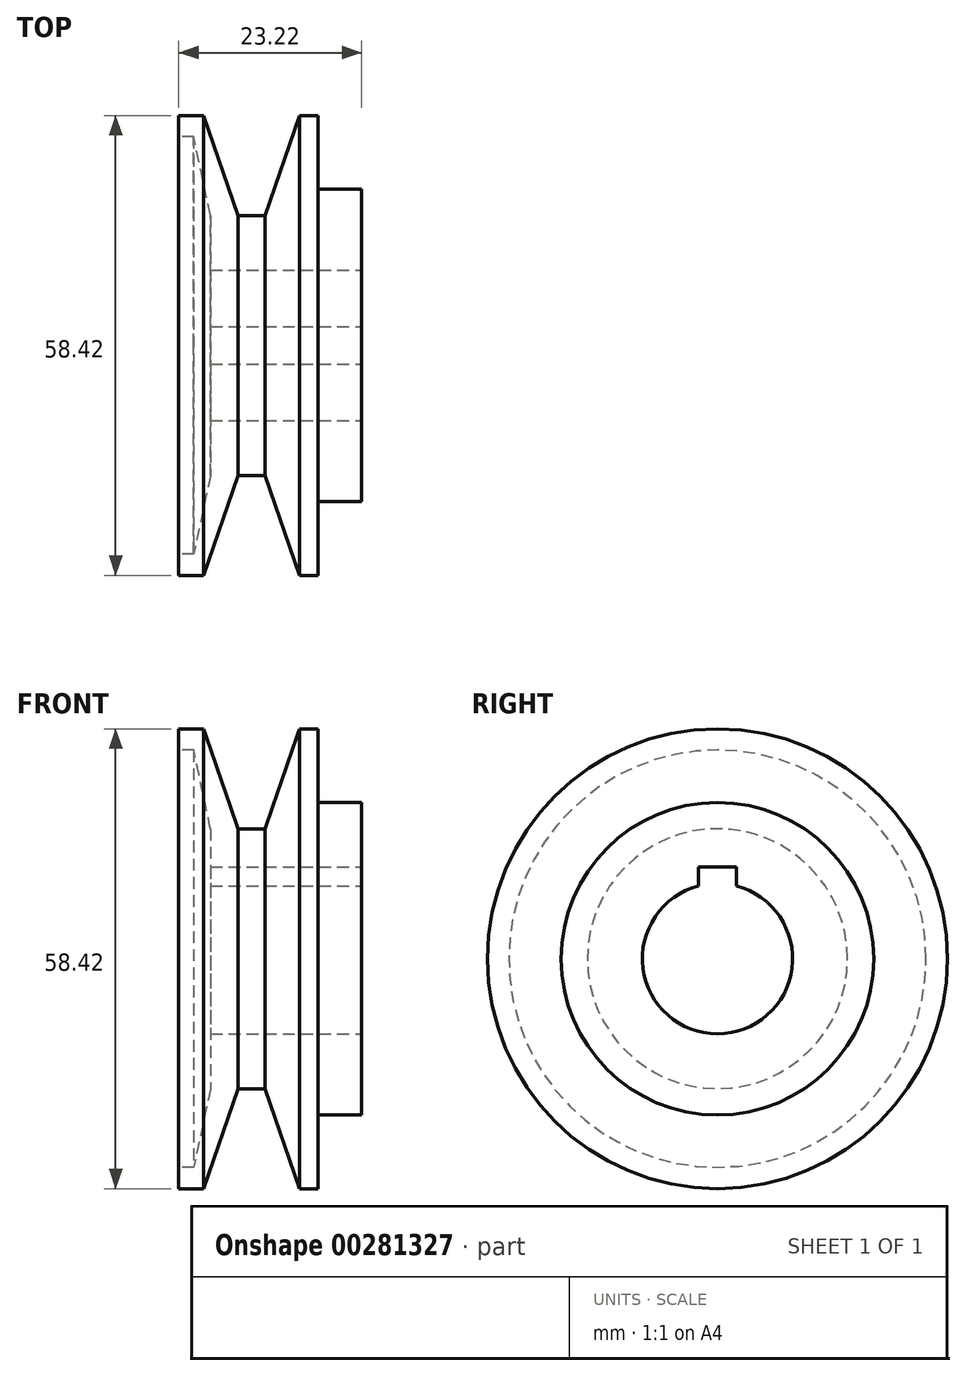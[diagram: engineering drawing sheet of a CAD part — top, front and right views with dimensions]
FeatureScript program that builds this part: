
annotation { "Feature Type Name" : "Feature", "Feature Type Description" : "" }
export const myFeature = defineFeature(function(context is Context, id is Id, definition is map)
    precondition{}
    {
        {
            var Q0;
            Q0=qCreatedBy(makeId("Front.planeOp"),FACE);
            var sketch = newSketch(context, id + "F0", { "sketchPlane" : qUnion([Q0])});
            skLineSegment(sketch, "E0", {"start": v(0, 0) * mm, "end": v(0.15, 0) * mm});
            skLineSegment(sketch, "E1", {"start": v(0.15, 0) * mm, "end": v(4.5, 12.7) * mm});
            skLineSegment(sketch, "E2", {"start": v(0, 0) * mm, "end": v(-3.3, 0) * mm});
            skLineSegment(sketch, "E3", {"start": v(-3.3, 0) * mm, "end": v(-7.7, 12.7) * mm});
            skLineSegment(sketch, "E4", {"start": v(-7.7, 12.7) * mm, "end": v(-10.83, 12.7) * mm});
            skLineSegment(sketch, "E5", {"start": v(-10.83, 12.7) * mm, "end": v(-10.83, 9.99) * mm});
            skLineSegment(sketch, "E6", {"start": v(-10.83, 9.99) * mm, "end": v(-8.93, 9.99) * mm});
            skLineSegment(sketch, "E7", {"start": v(-8.93, 9.99) * mm, "end": v(-6.8, 0) * mm});
            skLineSegment(sketch, "E8", {"start": v(-6.8, 0) * mm, "end": v(-6.8, -4.83) * mm});
            skLineSegment(sketch, "E9", {"start": v(4.5, 12.7) * mm, "end": v(6.83, 12.7) * mm});
            skLineSegment(sketch, "E10", {"start": v(6.83, 12.7) * mm, "end": v(6.83, -16.5) * mm});
            skPoint(sketch, "E11.orphan", {"position": v(6.83, -4.83) * mm});
            skLineSegment(sketch, "E12", {"start": v(-6.8, -4.83) * mm, "end": v(-6.8, -16.5) * mm});
            skLineSegment(sketch, "E13", {"start": v(-6.8, -16.5) * mm, "end": v(6.83, -16.5) * mm});
            skSolve(sketch);
        }
        {
            var Q0;
            Q0 = qSketchRegion(id + "F0", true);
            var Q1;
            Q1=sQuery(id+"F0.wireOp",EDGE,"E13");
            revolve(context, id + "F1", {"entities" : qUnion([Q0]), "axis" : qUnion([Q1]), "revolveType" : RevolveType.FULL});
        }
        {
            var Q0;
            Q0=makeQuery(id+"F1.opRevolve","SWEPT_FACE",FACE,{"disambiguationData":[OSD([sQuery(id+"F0.wireOp",EDGE,"E10")])]});
            var sketch = newSketch(context, id + "F2", { "sketchPlane" : qUnion([Q0])});
            skCircle(sketch, "E14", {"center": v(0, -16.5) * mm, "radius": 19.85 * mm});
            skSolve(sketch);
        }
        {
            var Q0;
            Q0=makeQuery(id+"F2.imprint","IMPRINT",FACE,{"disambiguationData":[TD([[makeQuery(id+"F2.imprint","IMPRINT",EDGE,{"derivedFrom":sQuery(id+"F2.wireOp",EDGE,"E14")}),1.0]])]});
            extrude(context, id + "F3", {"entities" : qUnion([Q0]), "operationType" : NewBodyOperationType.ADD, "depth" : 5.56 * mm});
        }
        {
            var Q0;
            Q0=makeQuery(id+"F3.opExtrude","CAP_FACE",FACE,{"disambiguationData":[OSD([sQuery(id+"F2.wireOp",EDGE,"E14")])],"isStart":false});
            var sketch = newSketch(context, id + "F4", { "sketchPlane" : qUnion([Q0])});
            skArc(sketch, "E15", {"start": v(-2.4, -7.26) * mm, "mid": v(0, -26.06) * mm, "end": v(2.4, -7.26) * mm});
            skPoint(sketch, "E16.endSnap0", {"position": v(0, -4.85) * mm});
            skLineSegment(sketch, "E17", {"start": v(0, -4.85) * mm, "end": v(2.4, -4.85) * mm});
            skLineSegment(sketch, "E18", {"start": v(2.4, -4.85) * mm, "end": v(2.4, -7.26) * mm});
            skLineSegment(sketch, "E19.MirrorCS", {"start": v(0, -4.85) * mm, "end": v(-2.4, -4.85) * mm});
            skLineSegment(sketch, "E20.MirrorCS", {"start": v(-2.4, -4.85) * mm, "end": v(-2.4, -7.26) * mm});
            skSolve(sketch);
        }
        {
            var Q0;
            Q0=makeQuery(id+"F4.imprint","IMPRINT",FACE,{"disambiguationData":[TD([[makeQuery(id+"F4.imprint","IMPRINT",EDGE,{"derivedFrom":sQuery(id+"F4.wireOp",EDGE,"E15")}),1.0]])]});
            extrude(context, id + "F5", {"entities" : qUnion([Q0]), "operationType" : NewBodyOperationType.REMOVE, "oppositeDirection" : true, "depth" : 254 * mm});
        }
    });
